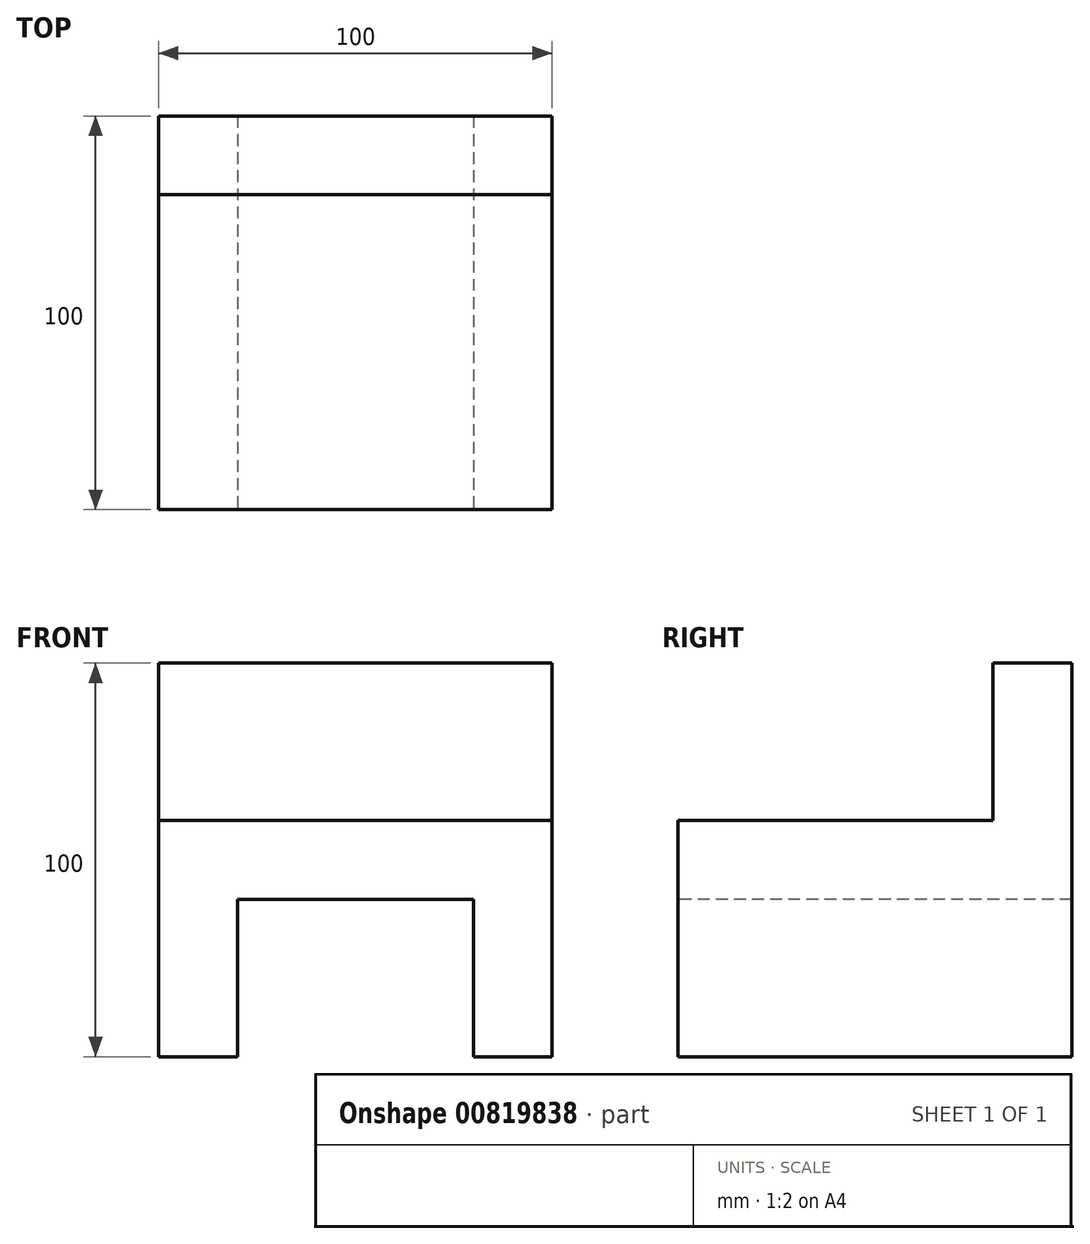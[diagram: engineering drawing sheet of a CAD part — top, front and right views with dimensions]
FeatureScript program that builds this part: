
annotation { "Feature Type Name" : "Feature", "Feature Type Description" : "" }
export const myFeature = defineFeature(function(context is Context, id is Id, definition is map)
    precondition{}
    {
        {
            var Q0;
            Q0=qCreatedBy(makeId("Top.planeOp"),FACE);
            var sketch = newSketch(context, id + "F0", { "sketchPlane" : qUnion([Q0])});
            skLineSegment(sketch, "E0.bottom", {"start": v(-50, 50) * mm, "end": v(50, 50) * mm});
            skLineSegment(sketch, "E0.top", {"start": v(-50, -50) * mm, "end": v(50, -50) * mm});
            skLineSegment(sketch, "E0.left", {"start": v(-50, 50) * mm, "end": v(-50, -50) * mm});
            skLineSegment(sketch, "E0.right", {"start": v(50, 50) * mm, "end": v(50, -50) * mm});
            skPoint(sketch, "E0.middle", {"position": v(0, 0) * mm});
            skSolve(sketch);
        }
        {
            var Q0;
            Q0 = qSketchRegion(id + "F0", true);
            extrude(context, id + "F1", {"entities" : qUnion([Q0]), "depth" : 100 * mm, "offsetDistance" : 25 * mm});
        }
        {
            var Q0;
            Q0=makeQuery(id+"F1.opExtrude","CAP_FACE",FACE,{"disambiguationData":[OSD([sQuery(id+"F0.wireOp",EDGE,"E0.bottom"),sQuery(id+"F0.wireOp",EDGE,"E0.top"),sQuery(id+"F0.wireOp",EDGE,"E0.left"),sQuery(id+"F0.wireOp",EDGE,"E0.right")])],"isStart":false});
            var sketch = newSketch(context, id + "F2", { "sketchPlane" : qUnion([Q0])});
            skLineSegment(sketch, "E1.bottom", {"start": v(-50, -50) * mm, "end": v(50, -50) * mm});
            skLineSegment(sketch, "E1.top", {"start": v(-50, 30) * mm, "end": v(50, 30) * mm});
            skLineSegment(sketch, "E1.left", {"start": v(-50, -50) * mm, "end": v(-50, 30) * mm});
            skLineSegment(sketch, "E1.right", {"start": v(50, -50) * mm, "end": v(50, 30) * mm});
            skSolve(sketch);
        }
        {
            var Q0;
            Q0 = qSketchRegion(id + "F2", true);
            extrude(context, id + "F3", {"entities" : qUnion([Q0]), "operationType" : NewBodyOperationType.REMOVE, "oppositeDirection" : true, "depth" : 40 * mm, "offsetDistance" : 25 * mm});
        }
        {
            var Q0;
            Q0=makeQuery(id+"F1.opExtrude","SWEPT_FACE",FACE,{"disambiguationData":[OSD([sQuery(id+"F0.wireOp",EDGE,"E0.top")])]});
            var sketch = newSketch(context, id + "F4", { "sketchPlane" : qUnion([Q0])});
            skLineSegment(sketch, "E2.bottom", {"start": v(-30, 0) * mm, "end": v(30, 0) * mm});
            skLineSegment(sketch, "E2.top", {"start": v(-30, 40) * mm, "end": v(30, 40) * mm});
            skLineSegment(sketch, "E2.left", {"start": v(-30, 0) * mm, "end": v(-30, 40) * mm});
            skLineSegment(sketch, "E2.right", {"start": v(30, 0) * mm, "end": v(30, 40) * mm});
            skSolve(sketch);
        }
        {
            var Q0;
            Q0 = qSketchRegion(id + "F4", true);
            extrude(context, id + "F5", {"entities" : qUnion([Q0]), "operationType" : NewBodyOperationType.REMOVE, "endBound" : BoundingType.THROUGH_ALL, "oppositeDirection" : true, "depth" : 25 * mm, "offsetDistance" : 25 * mm});
        }
    });
